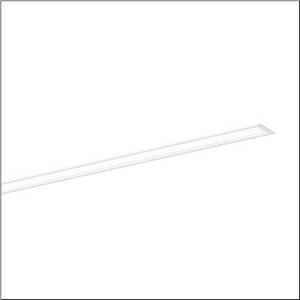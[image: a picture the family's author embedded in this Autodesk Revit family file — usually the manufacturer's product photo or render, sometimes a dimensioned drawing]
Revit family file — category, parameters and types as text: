
# Revit family: silica_21_51mx13tat4w
name_source: partatom
category: Lighting Fixtures
units: mm (PartAtom-declared; Revit-internal decimal feet)

## family parameters
Cut with Voids When Loaded = No
Host = Face
Light Source = No
Part Type = Normal
Room Calculation Point = No
Round Connector Dimension = Use Diameter
Shared = No

## types (1)
- --- (1 x LED, 3230 lm, 32.4 W, 6500K)
    Apparent Load = 32 VA
    CIE Flux Codes = 78 96 99 100 100
    Color Rendering = 80
    Color Temperature = 6500K
    Default Elevation = 1800 mm
    Description = Silica 21, office luminaire, primary optical cover: prismatic diffuser, of PMMA, CAT 2 (L<= 3000cd/m²), light emission: direct distribution, primary light characteristic: symmetric, installation type: recessed, LED, rated luminous flux: 3.230lm, luminous efficacy: 95lm/W, light colour: 8tw, colour temperature: 2700..6500K, control gear: DALI DT8, with terminal, 3+2-pole, max. 2.5mm², mains connection: 220..240V, AC, 50/60Hz, rated input power: 34W, luminaire housing, of aluminium, traffic white (RAL 9016), length: 1.228mm, width: 79mm, height: 53mm, protection rating (complete): IP20, insulation class (complete): insulation class I (protective earthing), certification: CE, ENEC, VDE, permissible operating ambient temperature: 0..+35°C, standard: EN 50419, packaging unit: 1 piece
    Height = 0 mm  [stored 0 ft]
    Lamp = 1 x LED
    Lamp Light Flux = 3230 lm
    Lamp Power = 32.4 W
    Lamp count = 1
    Length = 1227 mm
    Luminous efficacy = 100 lm/W
    Manufacturer = Siteco
    ModVariant = No
    Model = 51MX13TAT4W
    Mounting Place = Ceiling
    Mounting Type = Recessed
    Number of Poles = 1
    OnlyDefault = Yes
    Power Factor = 1
    Product Name = Silica 21
    Product group = office luminaire | ceiling recessed
    ProductGroupID = 400
    Protection Class = Protection class I
    Protection Degree = IP 20
    RLX_Detail_Level = 1
    RLX_Emergency_Light_Flux = 0 lm
    RLX_Emergency_Type = 0
    RLX_Emergency_Type_DB = No
    RlxData = <blob elided: 13065 chars, md5=8fbbd0c6>
    Socket = socket
    Standby Power = 0 W
    System Light Flux = 3230 lm
    System Power = 32 W
    Type Comments = individual setting
    Type Image = l_1335881.jpg
    URL = http://relux.com
    VarID = @adj_139349
    Voltage = 0 V
    Weight = 0.00 kg
    Width = 79 mm

note: [stored X ft] marks values corroborated as IEEE doubles in the binary element streams (Revit-internal decimal feet)

## geometry (parser evidence)
native form markers: Sweep x9
no freeform markers — native parametric forms only
